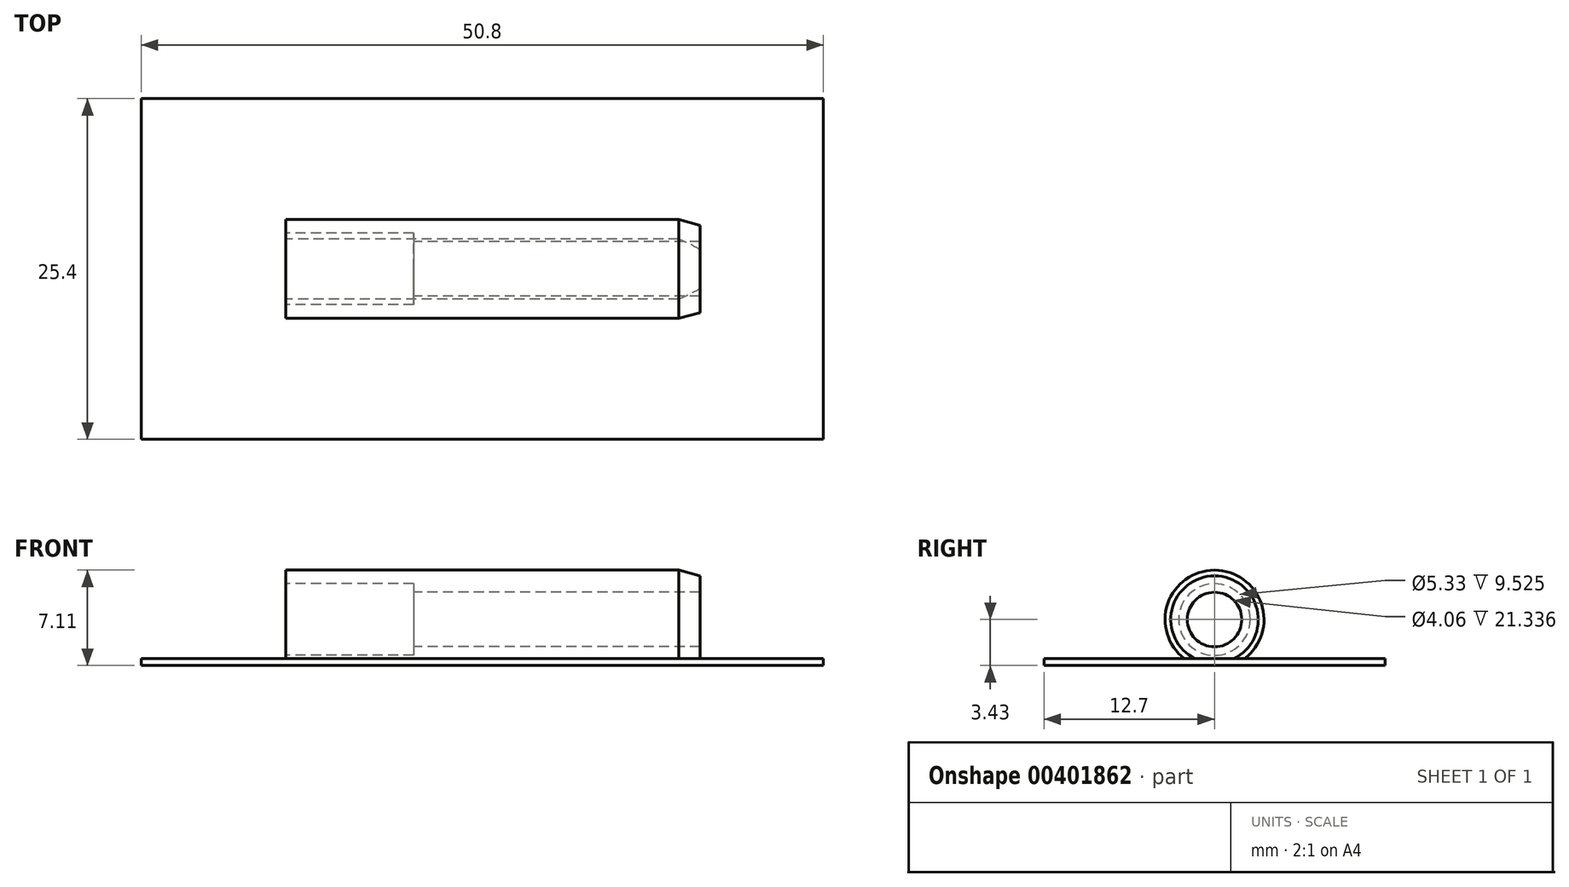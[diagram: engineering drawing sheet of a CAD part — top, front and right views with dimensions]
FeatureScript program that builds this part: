
annotation { "Feature Type Name" : "Feature", "Feature Type Description" : "" }
export const myFeature = defineFeature(function(context is Context, id is Id, definition is map)
    precondition{}
    {
        {
            var Q0;
            Q0=qCreatedBy(makeId("Front.planeOp"),FACE);
            var sketch = newSketch(context, id + "F0", { "sketchPlane" : qUnion([Q0])});
            skLineSegment(sketch, "E0", {"start": v(0, 2.67) * mm, "end": v(0, 3.68) * mm});
            skLineSegment(sketch, "E1", {"start": v(0, 3.68) * mm, "end": v(29.27, 3.68) * mm});
            skLineSegment(sketch, "E2", {"start": v(29.27, 3.68) * mm, "end": v(30.86, 3.26) * mm});
            skLineSegment(sketch, "E3", {"start": v(30.86, 3.26) * mm, "end": v(30.86, 2.03) * mm});
            skLineSegment(sketch, "E4", {"start": v(30.86, 2.03) * mm, "end": v(9.52, 2.03) * mm});
            skLineSegment(sketch, "E5", {"start": v(9.52, 2.03) * mm, "end": v(9.52, 2.67) * mm});
            skLineSegment(sketch, "E6", {"start": v(9.52, 2.67) * mm, "end": v(0, 2.67) * mm});
            skLineSegment(sketch, "E7", {"start": v(0, 0) * mm, "end": v(34.3, 0) * mm, "construction": true});
            skSolve(sketch);
        }
        {
            var Q0;
            Q0 = qSketchRegion(id + "F0", true);
            var Q1;
            Q1=sQuery(id+"F0.wireOp",EDGE,"E7");
            revolve(context, id + "F1", {"entities" : qUnion([Q0]), "axis" : qUnion([Q1]), "revolveType" : RevolveType.FULL});
        }
        {
            var Q0;
            Q0=makeQuery(id+"F1.opRevolve","SWEPT_FACE",FACE,{"disambiguationData":[OSD([sQuery(id+"F0.wireOp",EDGE,"E0")])]});
            var sketch = newSketch(context, id + "F2", { "sketchPlane" : qUnion([Q0])});
            skLineSegment(sketch, "E8", {"start": v(-2.24, -2.92) * mm, "end": v(2.24, -2.92) * mm});
            skLineSegment(sketch, "E9", {"start": v(2.24, -2.92) * mm, "end": v(2.24, -3.68) * mm});
            skLineSegment(sketch, "E10", {"start": v(2.24, -3.68) * mm, "end": v(-2.24, -3.68) * mm});
            skLineSegment(sketch, "E11", {"start": v(-2.24, -3.68) * mm, "end": v(-2.24, -2.92) * mm});
            skPoint(sketch, "E12", {"position": v(0, -2.67) * mm});
            skSolve(sketch);
        }
        {
            var Q0;
            Q0 = qSketchRegion(id + "F2", true);
            extrude(context, id + "F3", {"entities" : qUnion([Q0]), "operationType" : NewBodyOperationType.REMOVE, "endBound" : BoundingType.THROUGH_ALL, "oppositeDirection" : true, "depth" : 25.4 * mm});
        }
        {
            var Q0;
            Q0=makeQuery(id+"F3.boolean.opBoolean","COPY",FACE,{"derivedFrom":makeQuery(id+"F3.opExtrude","SWEPT_FACE",FACE,{"disambiguationData":[OSD([sQuery(id+"F2.wireOp",EDGE,"E8")])]})});
            var sketch = newSketch(context, id + "F4", { "sketchPlane" : qUnion([Q0])});
            skLineSegment(sketch, "E13.bottom", {"start": v(-10.76, -12.7) * mm, "end": v(40.04, -12.7) * mm});
            skLineSegment(sketch, "E13.top", {"start": v(-10.76, 12.7) * mm, "end": v(40.04, 12.7) * mm});
            skLineSegment(sketch, "E13.left", {"start": v(-10.76, -12.7) * mm, "end": v(-10.76, 12.7) * mm});
            skLineSegment(sketch, "E13.right", {"start": v(40.04, -12.7) * mm, "end": v(40.04, 12.7) * mm});
            skPoint(sketch, "E14", {"position": v(-10.76, 0) * mm});
            skPoint(sketch, "E15", {"position": v(14.64, 2.24) * mm});
            skPoint(sketch, "E16", {"position": v(14.64, 12.7) * mm});
            skSolve(sketch);
        }
        {
            var Q0;
            Q0 = qSketchRegion(id + "F4", true);
            extrude(context, id + "F5", {"entities" : qUnion([Q0]), "operationType" : NewBodyOperationType.ADD, "depth" : 0.5 * mm});
        }
    });
